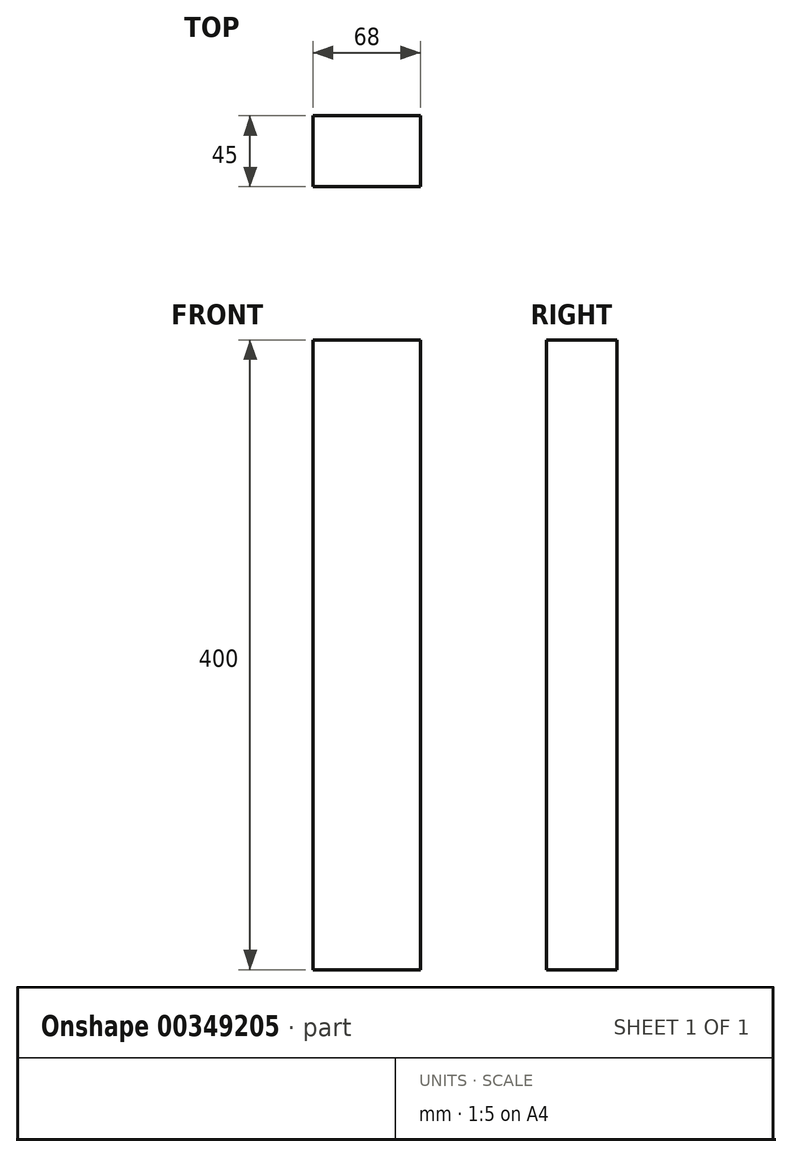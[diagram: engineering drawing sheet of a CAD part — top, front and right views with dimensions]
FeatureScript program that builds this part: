
annotation { "Feature Type Name" : "Feature", "Feature Type Description" : "" }
export const myFeature = defineFeature(function(context is Context, id is Id, definition is map)
    precondition{}
    {
        {
            var Q0;
            Q0=qCreatedBy(makeId("Front.planeOp"),FACE);
            var sketch = newSketch(context, id + "F0", { "sketchPlane" : qUnion([Q0])});
            skLineSegment(sketch, "E0.bottom", {"start": v(0, 0) * mm, "end": v(68, 0) * mm});
            skLineSegment(sketch, "E0.top", {"start": v(0, 400) * mm, "end": v(68, 400) * mm});
            skLineSegment(sketch, "E0.left", {"start": v(0, 0) * mm, "end": v(0, 400) * mm});
            skLineSegment(sketch, "E0.right", {"start": v(68, 0) * mm, "end": v(68, 400) * mm});
            skSolve(sketch);
        }
        {
            var Q0;
            Q0 = qSketchRegion(id + "F0", true);
            extrude(context, id + "F1", {"entities" : qUnion([Q0]), "depth" : 45 * mm});
        }
    });
